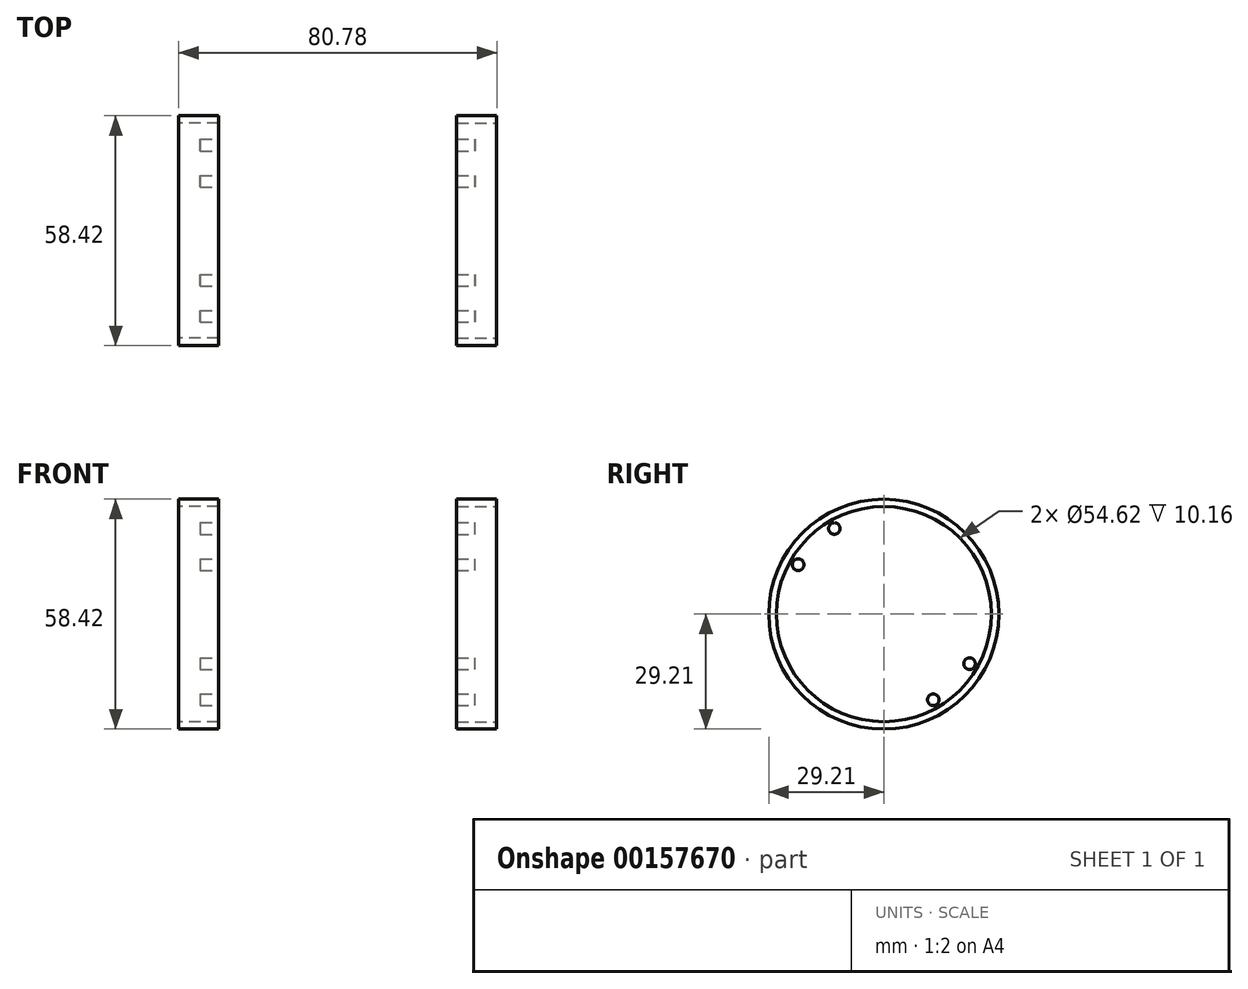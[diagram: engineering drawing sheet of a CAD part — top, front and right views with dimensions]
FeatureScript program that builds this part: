
annotation { "Feature Type Name" : "Feature", "Feature Type Description" : "" }
export const myFeature = defineFeature(function(context is Context, id is Id, definition is map)
    precondition{}
    {
        {
            var Q0;
            Q0=qCreatedBy(makeId("Right.planeOp"),FACE);
            var sketch = newSketch(context, id + "F0", { "sketchPlane" : qUnion([Q0])});
            skCircle(sketch, "E0", {"center": v(0, 0) * mm, "radius": 20.07 * mm});
            skSolve(sketch);
        }
        {
            var Q0;
            Q0=makeQuery(id+"F0.imprint","IMPRINT",FACE,{"disambiguationData":[TD([[makeQuery(id+"F0.imprint","IMPRINT",EDGE,{"derivedFrom":sQuery(id+"F0.wireOp",EDGE,"E0")}),1.0]])]});
            extrude(context, id + "F1", {"entities" : qUnion([Q0]), "depth" : 30.23 * mm, "hasSecondDirection" : true, "secondDirectionOppositeDirection" : true, "secondDirectionDepth" : 30.23 * mm});
        }
        {
            var Q0;
            Q0=makeQuery(id+"F1.opExtrude","CAP_FACE",FACE,{"disambiguationData":[OSD([sQuery(id+"F0.wireOp",EDGE,"E0")])],"isStart":false});
            var sketch = newSketch(context, id + "F2", { "sketchPlane" : qUnion([Q0])});
            skCircle(sketch, "E1", {"center": v(0, 0) * mm, "radius": 29.21 * mm});
            skSolve(sketch);
        }
        {
            var Q0;
            Q0=makeQuery(id+"F2.imprint","IMPRINT",FACE,{"disambiguationData":[TD([[makeQuery(id+"F2.imprint","IMPRINT",EDGE,{"derivedFrom":sQuery(id+"F2.wireOp",EDGE,"E1")}),1.0]])]});
            var Q1;
            Q1=makeQuery(id+"F2.imprint","IMPRINT",FACE,{"disambiguationData":[TD([[makeQuery(id+"F2.imprint","IMPRINT",EDGE,{"derivedFrom":makeQuery(id+"F1.opExtrude","CAP_EDGE",EDGE,{"disambiguationData":[OSD([sQuery(id+"F0.wireOp",EDGE,"E0")])],"isStart":false})}),1.0]])]});
            extrude(context, id + "F3", {"entities" : qUnion([Q0, Q1]), "operationType" : NewBodyOperationType.ADD, "depth" : 10.16 * mm});
        }
        {
            var Q0;
            Q0=makeQuery(id+"F1.opExtrude","CAP_FACE",FACE,{"disambiguationData":[OSD([sQuery(id+"F0.wireOp",EDGE,"E0")])],"isStart":true});
            var sketch = newSketch(context, id + "F4", { "sketchPlane" : qUnion([Q0])});
            skCircle(sketch, "E2", {"center": v(0, 0) * mm, "radius": 29.21 * mm});
            skSolve(sketch);
        }
        {
            var Q0;
            Q0=makeQuery(id+"F4.imprint","IMPRINT",FACE,{"disambiguationData":[TD([[makeQuery(id+"F4.imprint","IMPRINT",EDGE,{"derivedFrom":makeQuery(id+"F1.opExtrude","CAP_EDGE",EDGE,{"disambiguationData":[OSD([sQuery(id+"F0.wireOp",EDGE,"E0")])],"isStart":true})}),-1.0]])]});
            var Q1;
            Q1=makeQuery(id+"F4.imprint","IMPRINT",FACE,{"disambiguationData":[TD([[makeQuery(id+"F4.imprint","IMPRINT",EDGE,{"derivedFrom":sQuery(id+"F4.wireOp",EDGE,"E2")}),1.0]])]});
            extrude(context, id + "F5", {"entities" : qUnion([Q0, Q1]), "operationType" : NewBodyOperationType.ADD, "depth" : 10.16 * mm});
        }
        {
            var Q0;
            Q0=makeQuery(id+"F5.opExtrude","CAP_FACE",FACE,{"disambiguationData":[OSD([sQuery(id+"F4.wireOp",EDGE,"E2")])],"isStart":false});
            var sketch = newSketch(context, id + "F6", { "sketchPlane" : qUnion([Q0])});
            skCircle(sketch, "E3", {"center": v(0, 0) * mm, "radius": 27.31 * mm});
            skSolve(sketch);
        }
        {
            var Q0;
            Q0=makeQuery(id+"F6.imprint","IMPRINT",FACE,{"disambiguationData":[TD([[makeQuery(id+"F6.imprint","IMPRINT",EDGE,{"derivedFrom":sQuery(id+"F6.wireOp",EDGE,"E3")}),1.0]])]});
            extrude(context, id + "F7", {"entities" : qUnion([Q0]), "operationType" : NewBodyOperationType.REMOVE, "oppositeDirection" : true, "depth" : 5.46 * mm});
        }
        {
            var Q0;
            Q0=makeQuery(id+"F3.opExtrude","CAP_FACE",FACE,{"disambiguationData":[OSD([sQuery(id+"F2.wireOp",EDGE,"E1")])],"isStart":false});
            var sketch = newSketch(context, id + "F8", { "sketchPlane" : qUnion([Q0])});
            skCircle(sketch, "E4", {"center": v(0, 0) * mm, "radius": 27.31 * mm});
            skSolve(sketch);
        }
        {
            var Q0;
            Q0=makeQuery(id+"F8.imprint","IMPRINT",FACE,{"disambiguationData":[TD([[makeQuery(id+"F8.imprint","IMPRINT",EDGE,{"derivedFrom":sQuery(id+"F8.wireOp",EDGE,"E4")}),1.0]])]});
            extrude(context, id + "F9", {"entities" : qUnion([Q0]), "operationType" : NewBodyOperationType.REMOVE, "oppositeDirection" : true, "depth" : 5.46 * mm});
        }
        {
            var Q0;
            Q0=makeQuery(id+"F9.boolean.opBoolean","COPY",FACE,{"derivedFrom":makeQuery(id+"F9.opExtrude","CAP_FACE",FACE,{"disambiguationData":[OSD([sQuery(id+"F8.wireOp",EDGE,"E4")])],"isStart":false})});
            var sketch = newSketch(context, id + "F10", { "sketchPlane" : qUnion([Q0])});
            skCircle(sketch, "E5", {"center": v(0, 0) * mm, "radius": 16.9 * mm});
            skSolve(sketch);
        }
        {
            var Q0;
            Q0=makeQuery(id+"F10.imprint","IMPRINT",FACE,{"disambiguationData":[TD([[makeQuery(id+"F10.imprint","IMPRINT",EDGE,{"derivedFrom":sQuery(id+"F10.wireOp",EDGE,"E5")}),1.0]])]});
            extrude(context, id + "F11", {"entities" : qUnion([Q0]), "operationType" : NewBodyOperationType.REMOVE, "endBound" : BoundingType.THROUGH_ALL, "oppositeDirection" : true, "depth" : 76.2 * mm});
        }
        {
            var Q0;
            Q0=makeQuery(id+"F9.boolean.opBoolean","COPY",FACE,{"derivedFrom":makeQuery(id+"F9.opExtrude","CAP_FACE",FACE,{"disambiguationData":[OSD([sQuery(id+"F8.wireOp",EDGE,"E4")])],"isStart":false})});
            var sketch = newSketch(context, id + "F12", { "sketchPlane" : qUnion([Q0])});
            skCircle(sketch, "E6", {"center": v(12.57, 21.77) * mm, "radius": 1.47 * mm});
            skCircle(sketch, "E7", {"center": v(21.77, 12.57) * mm, "radius": 1.47 * mm});
            skCircle(sketch, "E8.MirrorC", {"center": v(-12.57, 21.77) * mm, "radius": 1.47 * mm});
            skCircle(sketch, "E9.MirrorC", {"center": v(-21.77, 12.57) * mm, "radius": 1.47 * mm});
            skCircle(sketch, "E10.MirrorC", {"center": v(-21.77, -12.57) * mm, "radius": 1.47 * mm});
            skCircle(sketch, "E11.MirrorC", {"center": v(-12.57, -21.77) * mm, "radius": 1.47 * mm});
            skCircle(sketch, "E12.MirrorC", {"center": v(12.57, -21.77) * mm, "radius": 1.47 * mm});
            skCircle(sketch, "E13.MirrorC", {"center": v(21.77, -12.57) * mm, "radius": 1.47 * mm});
            skSolve(sketch);
        }
        {
            var Q0;
            Q0=makeQuery(id+"F12.imprint","IMPRINT",FACE,{"disambiguationData":[TD([[makeQuery(id+"F12.imprint","IMPRINT",EDGE,{"derivedFrom":sQuery(id+"F12.wireOp",EDGE,"E9.MirrorC")}),-1.0]])]});
            var Q1;
            Q1=makeQuery(id+"F12.imprint","IMPRINT",FACE,{"disambiguationData":[TD([[makeQuery(id+"F12.imprint","IMPRINT",EDGE,{"derivedFrom":sQuery(id+"F12.wireOp",EDGE,"E8.MirrorC")}),-1.0]])]});
            var Q2;
            Q2=makeQuery(id+"F12.imprint","IMPRINT",FACE,{"disambiguationData":[TD([[makeQuery(id+"F12.imprint","IMPRINT",EDGE,{"derivedFrom":sQuery(id+"F12.wireOp",EDGE,"E6")}),1.0]])]});
            var Q3;
            Q3=makeQuery(id+"F12.imprint","IMPRINT",FACE,{"disambiguationData":[TD([[makeQuery(id+"F12.imprint","IMPRINT",EDGE,{"derivedFrom":sQuery(id+"F12.wireOp",EDGE,"E7")}),1.0]])]});
            var Q4;
            Q4=makeQuery(id+"F12.imprint","IMPRINT",FACE,{"disambiguationData":[TD([[makeQuery(id+"F12.imprint","IMPRINT",EDGE,{"derivedFrom":sQuery(id+"F12.wireOp",EDGE,"E13.MirrorC")}),-1.0]])]});
            var Q5;
            Q5=makeQuery(id+"F12.imprint","IMPRINT",FACE,{"disambiguationData":[TD([[makeQuery(id+"F12.imprint","IMPRINT",EDGE,{"derivedFrom":sQuery(id+"F12.wireOp",EDGE,"E12.MirrorC")}),-1.0]])]});
            var Q6;
            Q6=makeQuery(id+"F12.imprint","IMPRINT",FACE,{"disambiguationData":[TD([[makeQuery(id+"F12.imprint","IMPRINT",EDGE,{"derivedFrom":sQuery(id+"F12.wireOp",EDGE,"E11.MirrorC")}),1.0]])]});
            var Q7;
            Q7=makeQuery(id+"F12.imprint","IMPRINT",FACE,{"disambiguationData":[TD([[makeQuery(id+"F12.imprint","IMPRINT",EDGE,{"derivedFrom":sQuery(id+"F12.wireOp",EDGE,"E10.MirrorC")}),1.0]])]});
            extrude(context, id + "F13", {"entities" : qUnion([Q0, Q1, Q2, Q3, Q4, Q5, Q6, Q7]), "operationType" : NewBodyOperationType.REMOVE, "endBound" : BoundingType.THROUGH_ALL, "oppositeDirection" : true, "depth" : 25.4 * mm});
        }
        {
            var Q0;
            Q0=qCreatedBy(makeId("Top.planeOp"),FACE);
            cPlane(context, id + "F14", {"entities" : qUnion([Q0]), "cplaneType" : CPlaneType.OFFSET, "offset" : 20.07 * mm, "width" : 152.4 * mm, "height" : 152.4 * mm});
        }
        {
            var Q0;
            Q0=qCreatedBy(id+"F14.planeOp",FACE);
            var sketch = newSketch(context, id + "F15", { "sketchPlane" : qUnion([Q0])});
            skLineSegment(sketch, "E14.bottom", {"start": v(-19.05, 30.23) * mm, "end": v(19.05, 30.23) * mm});
            skLineSegment(sketch, "E14.top", {"start": v(-6.35, 11.18) * mm, "end": v(6.35, 11.18) * mm});
            skLineSegment(sketch, "E14.left", {"start": v(-19.05, 30.23) * mm, "end": v(-19.05, 23.88) * mm});
            skLineSegment(sketch, "E14.right", {"start": v(19.05, 30.23) * mm, "end": v(19.05, 23.88) * mm});
            skLineSegment(sketch, "E15.bottom", {"start": v(-6.35, -11.18) * mm, "end": v(6.35, -11.18) * mm});
            skLineSegment(sketch, "E15.top", {"start": v(-19.05, -30.23) * mm, "end": v(19.05, -30.23) * mm});
            skLineSegment(sketch, "E15.left", {"start": v(-19.05, -23.88) * mm, "end": v(-19.05, -30.23) * mm});
            skLineSegment(sketch, "E15.right", {"start": v(19.05, -23.88) * mm, "end": v(19.05, -30.23) * mm});
            skPoint(sketch, "E16.visualSharp", {"position": v(-19.05, 11.18) * mm});
            skArc(sketch, "E16.filletArc", {"start": v(-19.05, 23.88) * mm, "mid": v(-15.33, 14.9) * mm, "end": v(-6.35, 11.18) * mm});
            skPoint(sketch, "E17.visualSharp", {"position": v(19.05, 11.18) * mm});
            skArc(sketch, "E17.filletArc", {"start": v(6.35, 11.18) * mm, "mid": v(15.33, 14.9) * mm, "end": v(19.05, 23.88) * mm});
            skPoint(sketch, "E18.visualSharp", {"position": v(-19.05, -11.18) * mm});
            skArc(sketch, "E18.filletArc", {"start": v(-6.35, -11.18) * mm, "mid": v(-15.33, -14.9) * mm, "end": v(-19.05, -23.88) * mm});
            skPoint(sketch, "E19.visualSharp", {"position": v(19.05, -11.18) * mm});
            skArc(sketch, "E19.filletArc", {"start": v(19.05, -23.88) * mm, "mid": v(15.33, -14.9) * mm, "end": v(6.35, -11.18) * mm});
            skSolve(sketch);
        }
        {
            var Q0;
            Q0=makeQuery(id+"F15.imprint","IMPRINT",FACE,{"disambiguationData":[TD([[makeQuery(id+"F15.imprint","IMPRINT",EDGE,{"derivedFrom":sQuery(id+"F15.wireOp",EDGE,"E14.bottom")}),-1.0]])]});
            var Q1;
            Q1=makeQuery(id+"F15.imprint","IMPRINT",FACE,{"disambiguationData":[TD([[makeQuery(id+"F15.imprint","IMPRINT",EDGE,{"derivedFrom":sQuery(id+"F15.wireOp",EDGE,"E15.bottom")}),-1.0]])]});
            extrude(context, id + "F16", {"entities" : qUnion([Q0, Q1]), "operationType" : NewBodyOperationType.REMOVE, "endBound" : BoundingType.THROUGH_ALL, "oppositeDirection" : true, "depth" : 25.4 * mm});
        }
    });
